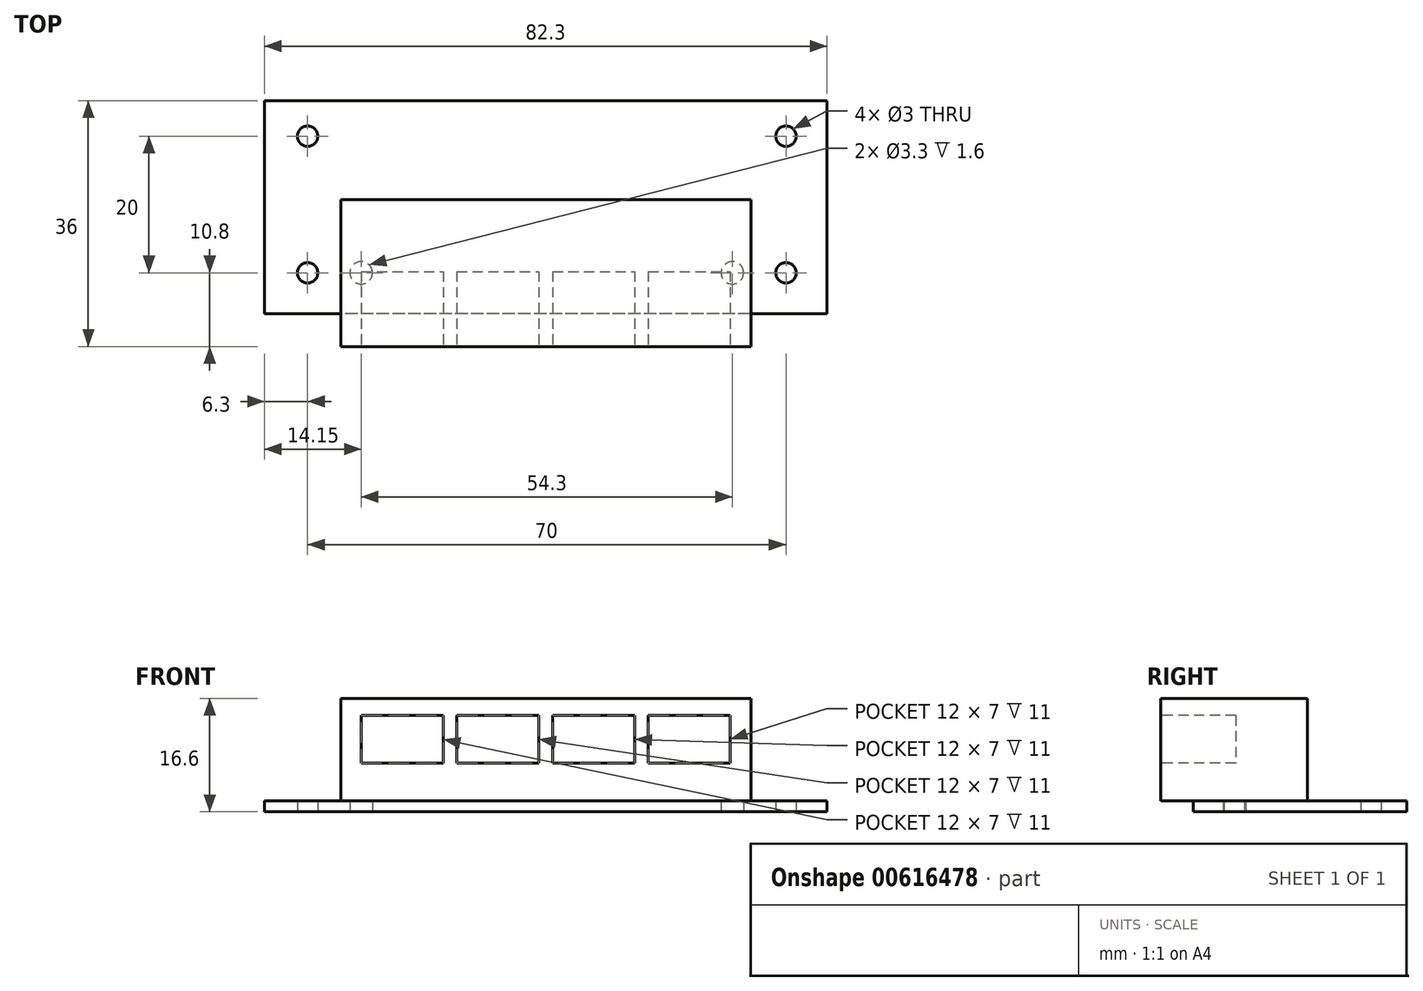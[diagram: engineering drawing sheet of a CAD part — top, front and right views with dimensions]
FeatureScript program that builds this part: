
annotation { "Feature Type Name" : "Feature", "Feature Type Description" : "" }
export const myFeature = defineFeature(function(context is Context, id is Id, definition is map)
    precondition{}
    {
        {
            var Q0;
            Q0=qCreatedBy(makeId("Top.planeOp"),FACE);
            var sketch = newSketch(context, id + "F0", { "sketchPlane" : qUnion([Q0])});
            skLineSegment(sketch, "E0.bottom", {"start": v(41.15, -15.6) * mm, "end": v(-41.15, -15.6) * mm});
            skLineSegment(sketch, "E0.top", {"start": v(41.15, 15.6) * mm, "end": v(-41.15, 15.6) * mm});
            skLineSegment(sketch, "E0.left", {"start": v(41.15, -15.6) * mm, "end": v(41.15, 15.6) * mm});
            skLineSegment(sketch, "E0.right", {"start": v(-41.15, -15.6) * mm, "end": v(-41.15, 15.6) * mm});
            skPoint(sketch, "E0.middle", {"position": v(0, 0) * mm});
            skCircle(sketch, "E1", {"center": v(-34.85, 10.4) * mm, "radius": 1.5 * mm});
            skCircle(sketch, "E2", {"center": v(-34.85, -9.6) * mm, "radius": 1.5 * mm});
            skCircle(sketch, "E3", {"center": v(35.15, 10.4) * mm, "radius": 1.5 * mm});
            skCircle(sketch, "E4", {"center": v(35.15, -9.6) * mm, "radius": 1.5 * mm});
            skCircle(sketch, "E5", {"center": v(-27, -9.6) * mm, "radius": 1.65 * mm});
            skCircle(sketch, "E6", {"center": v(27.3, -9.6) * mm, "radius": 1.65 * mm});
            skLineSegment(sketch, "E7", {"start": v(-56.96, 10.4) * mm, "end": v(54.56, 10.4) * mm, "construction": true});
            skLineSegment(sketch, "E8", {"start": v(54.56, -9.6) * mm, "end": v(-57.28, -9.6) * mm, "construction": true});
            skLineSegment(sketch, "E9", {"start": v(-34.85, -24.03) * mm, "end": v(-34.85, 26.12) * mm, "construction": true});
            skLineSegment(sketch, "E10", {"start": v(35.15, 26.12) * mm, "end": v(35.15, -24.83) * mm, "construction": true});
            skSolve(sketch);
        }
        {
            var Q0;
            Q0=makeQuery(id+"F0.imprint","IMPRINT",FACE,{"disambiguationData":[TD([[makeQuery(id+"F0.imprint","IMPRINT",EDGE,{"derivedFrom":sQuery(id+"F0.wireOp",EDGE,"E0.bottom")}),-1.0]])]});
            extrude(context, id + "F1", {"entities" : qUnion([Q0]), "depth" : 1.6 * mm, "offsetDistance" : 25 * mm});
        }
        {
            var Q0;
            Q0=makeQuery(id+"F1.opExtrude","CAP_FACE",FACE,{"disambiguationData":[OSD([sQuery(id+"F0.wireOp",EDGE,"E0.bottom"),sQuery(id+"F0.wireOp",EDGE,"E0.top"),sQuery(id+"F0.wireOp",EDGE,"E0.left"),sQuery(id+"F0.wireOp",EDGE,"E0.right"),sQuery(id+"F0.wireOp",EDGE,"E1"),sQuery(id+"F0.wireOp",EDGE,"E2"),sQuery(id+"F0.wireOp",EDGE,"E3"),sQuery(id+"F0.wireOp",EDGE,"E4"),sQuery(id+"F0.wireOp",EDGE,"E5"),sQuery(id+"F0.wireOp",EDGE,"E6")])],"isStart":false});
            var sketch = newSketch(context, id + "F2", { "sketchPlane" : qUnion([Q0])});
            skLineSegment(sketch, "E11.bottom", {"start": v(-30, 1.1) * mm, "end": v(30, 1.1) * mm});
            skLineSegment(sketch, "E11.top", {"start": v(-30, -20.4) * mm, "end": v(30, -20.4) * mm});
            skLineSegment(sketch, "E11.left", {"start": v(-30, 1.1) * mm, "end": v(-30, -20.4) * mm});
            skLineSegment(sketch, "E11.right", {"start": v(30, 1.1) * mm, "end": v(30, -20.4) * mm});
            skPoint(sketch, "E11.middle", {"position": v(0, -9.65) * mm});
            skSolve(sketch);
        }
        {
            var Q0;
            {var subQ1=sQuery(id+"F2.wireOp",EDGE,"E11.bottom");Q0=makeQuery(id+"F2.imprint","IMPRINT",FACE,{"disambiguationData":[TD([[makeQuery(id+"F2.imprint","IMPRINT",EDGE,{"derivedFrom":subQ1}),-1.0]])]});}
            var Q1;
            {var subQ0=sQuery(id+"F2.wireOp",EDGE,"E11.top");Q1=makeQuery(id+"F2.imprint","IMPRINT",FACE,{"disambiguationData":[TD([[makeQuery(id+"F2.imprint","IMPRINT",EDGE,{"derivedFrom":subQ0}),1.0]])]});}
            var Q2;
            Q2=makeQuery(id+"F2.imprint","IMPRINT",FACE,{"disambiguationData":[TD([[makeQuery(id+"F2.imprint","IMPRINT",EDGE,{"derivedFrom":makeQuery(id+"F1.opExtrude","CAP_EDGE",EDGE,{"disambiguationData":[OSD([sQuery(id+"F0.wireOp",EDGE,"E5")])],"isStart":false})}),1.0]])]});
            var Q3;
            Q3=makeQuery(id+"F2.imprint","IMPRINT",FACE,{"disambiguationData":[TD([[makeQuery(id+"F2.imprint","IMPRINT",EDGE,{"derivedFrom":makeQuery(id+"F1.opExtrude","CAP_EDGE",EDGE,{"disambiguationData":[OSD([sQuery(id+"F0.wireOp",EDGE,"E6")])],"isStart":false})}),1.0]])]});
            extrude(context, id + "F3", {"entities" : qUnion([Q0, Q1, Q2, Q3]), "operationType" : NewBodyOperationType.ADD, "depth" : 15 * mm, "offsetDistance" : 25 * mm});
        }
        {
            var Q0;
            Q0=makeQuery(id+"F3.opExtrude","SWEPT_FACE",FACE,{"disambiguationData":[OSD([sQuery(id+"F2.wireOp",EDGE,"E11.top")])]});
            var sketch = newSketch(context, id + "F4", { "sketchPlane" : qUnion([Q0])});
            skLineSegment(sketch, "E12.bottom", {"start": v(-27, 14.1) * mm, "end": v(-15, 14.1) * mm});
            skLineSegment(sketch, "E12.top", {"start": v(-27, 7.1) * mm, "end": v(-15, 7.1) * mm});
            skLineSegment(sketch, "E12.left", {"start": v(-27, 14.1) * mm, "end": v(-27, 7.1) * mm});
            skLineSegment(sketch, "E12.right", {"start": v(-15, 14.1) * mm, "end": v(-15, 7.1) * mm});
            skLineSegment(sketch, "E13.bottom", {"start": v(-24.15, 7.1) * mm, "end": v(-17.85, 7.1) * mm});
            skLineSegment(sketch, "E13.top", {"start": v(-24.15, 5.1) * mm, "end": v(-17.85, 5.1) * mm});
            skLineSegment(sketch, "E13.left", {"start": v(-24.15, 7.1) * mm, "end": v(-24.15, 5.1) * mm});
            skLineSegment(sketch, "E13.right", {"start": v(-17.85, 7.1) * mm, "end": v(-17.85, 5.1) * mm});
            skLineSegment(sketch, "E14.bottom", {"start": v(-13, 14.1) * mm, "end": v(-1, 14.1) * mm});
            skLineSegment(sketch, "E14.top", {"start": v(-13, 7.1) * mm, "end": v(-1, 7.1) * mm});
            skLineSegment(sketch, "E14.left", {"start": v(-13, 14.1) * mm, "end": v(-13, 7.1) * mm});
            skLineSegment(sketch, "E14.right", {"start": v(-1, 14.1) * mm, "end": v(-1, 7.1) * mm});
            skLineSegment(sketch, "E15.bottom", {"start": v(-10.15, 7.1) * mm, "end": v(-3.85, 7.1) * mm});
            skLineSegment(sketch, "E15.top", {"start": v(-10.15, 5.1) * mm, "end": v(-3.85, 5.1) * mm});
            skLineSegment(sketch, "E15.left", {"start": v(-10.15, 7.1) * mm, "end": v(-10.15, 5.1) * mm});
            skLineSegment(sketch, "E15.right", {"start": v(-3.85, 7.1) * mm, "end": v(-3.85, 5.1) * mm});
            skLineSegment(sketch, "E16.bottom", {"start": v(15, 14.1) * mm, "end": v(27, 14.1) * mm});
            skLineSegment(sketch, "E16.top", {"start": v(15, 7.1) * mm, "end": v(27, 7.1) * mm});
            skLineSegment(sketch, "E16.left", {"start": v(15, 14.1) * mm, "end": v(15, 7.1) * mm});
            skLineSegment(sketch, "E16.right", {"start": v(27, 14.1) * mm, "end": v(27, 7.1) * mm});
            skLineSegment(sketch, "E17.bottom", {"start": v(17.85, 7.1) * mm, "end": v(24.15, 7.1) * mm});
            skLineSegment(sketch, "E17.top", {"start": v(17.85, 5.1) * mm, "end": v(24.15, 5.1) * mm});
            skLineSegment(sketch, "E17.left", {"start": v(17.85, 7.1) * mm, "end": v(17.85, 5.1) * mm});
            skLineSegment(sketch, "E17.right", {"start": v(24.15, 7.1) * mm, "end": v(24.15, 5.1) * mm});
            skLineSegment(sketch, "E18.bottom", {"start": v(1, 14.1) * mm, "end": v(13, 14.1) * mm});
            skLineSegment(sketch, "E18.top", {"start": v(1, 7.1) * mm, "end": v(13, 7.1) * mm});
            skLineSegment(sketch, "E18.left", {"start": v(1, 14.1) * mm, "end": v(1, 7.1) * mm});
            skLineSegment(sketch, "E18.right", {"start": v(13, 14.1) * mm, "end": v(13, 7.1) * mm});
            skLineSegment(sketch, "E19.bottom", {"start": v(3.85, 7.1) * mm, "end": v(10.15, 7.1) * mm});
            skLineSegment(sketch, "E19.top", {"start": v(3.85, 5.1) * mm, "end": v(10.15, 5.1) * mm});
            skLineSegment(sketch, "E19.left", {"start": v(3.85, 7.1) * mm, "end": v(3.85, 5.1) * mm});
            skLineSegment(sketch, "E19.right", {"start": v(10.15, 7.1) * mm, "end": v(10.15, 5.1) * mm});
            skLineSegment(sketch, "E20", {"start": v(-35.92, 14.1) * mm, "end": v(37.76, 14.1) * mm, "construction": true});
            skSolve(sketch);
        }
        {
            var Q0;
            Q0=makeQuery(id+"F4.imprint","IMPRINT",FACE,{"disambiguationData":[TD([[makeQuery(id+"F4.imprint","IMPRINT",EDGE,{"derivedFrom":sQuery(id+"F4.wireOp",EDGE,"E12.bottom")}),-1.0]])]});
            var Q1;
            Q1=makeQuery(id+"F4.imprint","IMPRINT",FACE,{"disambiguationData":[TD([[makeQuery(id+"F4.imprint","IMPRINT",EDGE,{"derivedFrom":sQuery(id+"F4.wireOp",EDGE,"E14.bottom")}),-1.0]])]});
            var Q2;
            Q2=makeQuery(id+"F4.imprint","IMPRINT",FACE,{"disambiguationData":[TD([[makeQuery(id+"F4.imprint","IMPRINT",EDGE,{"derivedFrom":sQuery(id+"F4.wireOp",EDGE,"E18.bottom")}),-1.0]])]});
            var Q3;
            Q3=makeQuery(id+"F4.imprint","IMPRINT",FACE,{"disambiguationData":[TD([[makeQuery(id+"F4.imprint","IMPRINT",EDGE,{"derivedFrom":sQuery(id+"F4.wireOp",EDGE,"E16.bottom")}),-1.0]])]});
            var Q4;
            Q4=makeQuery(id+"F4.imprint","IMPRINT",FACE,{"disambiguationData":[TD([[makeQuery(id+"F4.imprint","IMPRINT",EDGE,{"derivedFrom":sQuery(id+"F4.wireOp",EDGE,"E17.bottom")}),-1.0]])]});
            var Q5;
            Q5=makeQuery(id+"F4.imprint","IMPRINT",FACE,{"disambiguationData":[TD([[makeQuery(id+"F4.imprint","IMPRINT",EDGE,{"derivedFrom":sQuery(id+"F4.wireOp",EDGE,"E19.bottom")}),-1.0]])]});
            var Q6;
            Q6=makeQuery(id+"F4.imprint","IMPRINT",FACE,{"disambiguationData":[TD([[makeQuery(id+"F4.imprint","IMPRINT",EDGE,{"derivedFrom":sQuery(id+"F4.wireOp",EDGE,"E15.bottom")}),-1.0]])]});
            var Q7;
            Q7=makeQuery(id+"F4.imprint","IMPRINT",FACE,{"disambiguationData":[TD([[makeQuery(id+"F4.imprint","IMPRINT",EDGE,{"derivedFrom":sQuery(id+"F4.wireOp",EDGE,"E13.bottom")}),-1.0]])]});
            extrude(context, id + "F5", {"entities" : qUnion([Q0, Q1, Q2, Q3, Q4, Q5, Q6, Q7]), "operationType" : NewBodyOperationType.REMOVE, "oppositeDirection" : true, "depth" : 11 * mm, "offsetDistance" : 25 * mm});
        }
    });
